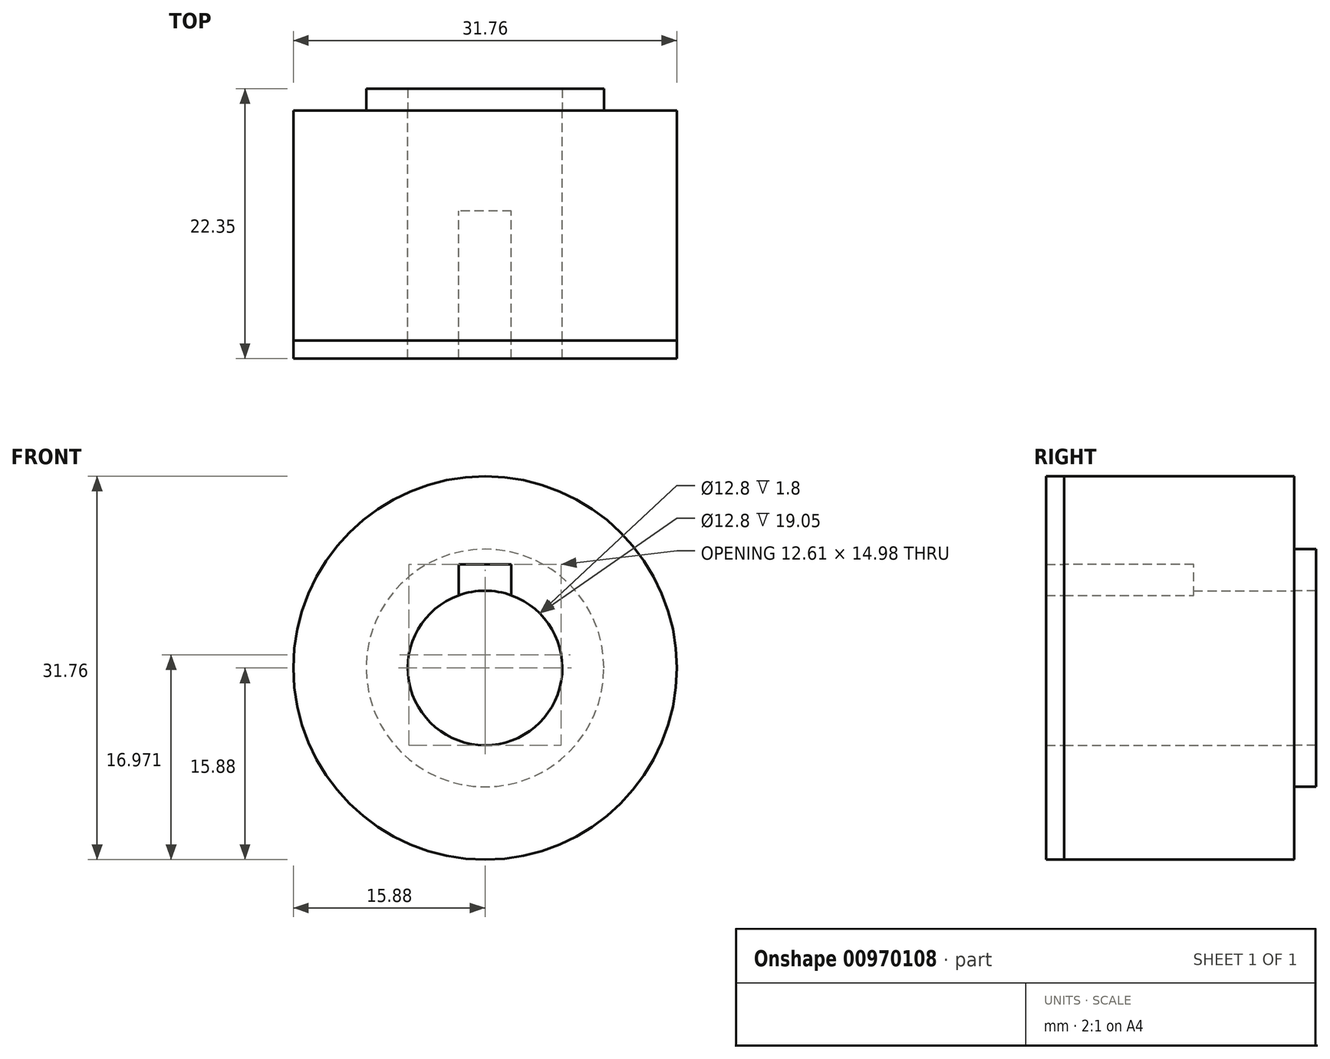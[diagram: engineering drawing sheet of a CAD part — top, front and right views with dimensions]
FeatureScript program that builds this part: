
annotation { "Feature Type Name" : "Feature", "Feature Type Description" : "" }
export const myFeature = defineFeature(function(context is Context, id is Id, definition is map)
    precondition{}
    {
        {
            var Q0;
            Q0=qCreatedBy(makeId("Front.planeOp"),FACE);
            var sketch = newSketch(context, id + "F0", { "sketchPlane" : qUnion([Q0])});
            skCircle(sketch, "E0", {"center": v(0, 0) * mm, "radius": 15.88 * mm});
            skCircle(sketch, "E1", {"center": v(0, 0) * mm, "radius": 6.4 * mm});
            skSolve(sketch);
        }
        {
            var Q0;
            Q0 = qSketchRegion(id + "F0", true);
            extrude(context, id + "F1", {"entities" : qUnion([Q0]), "depth" : 19.05 * mm, "offsetDistance" : 25.4 * mm});
        }
        {
            var Q0;
            Q0=makeQuery(id+"F1.opExtrude","CAP_FACE",FACE,{"disambiguationData":[OSD([sQuery(id+"F0.wireOp",EDGE,"E0"),sQuery(id+"F0.wireOp",EDGE,"E1")])],"isStart":false});
            var sketch = newSketch(context, id + "F2", { "sketchPlane" : qUnion([Q0])});
            skLineSegment(sketch, "E2", {"start": v(0, 6.4) * mm, "end": v(0, 4.22) * mm, "construction": true});
            skLineSegment(sketch, "E3.bottom", {"start": v(2.18, 4.22) * mm, "end": v(-2.18, 4.22) * mm});
            skLineSegment(sketch, "E3.top", {"start": v(2.18, 8.58) * mm, "end": v(-2.18, 8.58) * mm});
            skLineSegment(sketch, "E3.left", {"start": v(2.18, 4.22) * mm, "end": v(2.18, 8.58) * mm});
            skLineSegment(sketch, "E3.right", {"start": v(-2.18, 4.22) * mm, "end": v(-2.18, 8.58) * mm});
            skPoint(sketch, "E3.middle", {"position": v(0, 6.4) * mm});
            skSolve(sketch);
        }
        {
            var Q0;
            Q0 = qSketchRegion(id + "F2", true);
            extrude(context, id + "F3", {"entities" : qUnion([Q0]), "operationType" : NewBodyOperationType.REMOVE, "oppositeDirection" : true, "depth" : 10.72 * mm, "offsetDistance" : 25.4 * mm});
        }
        {
            var Q0;
            Q0=makeQuery(id+"F1.opExtrude","CAP_FACE",FACE,{"disambiguationData":[OSD([sQuery(id+"F0.wireOp",EDGE,"E0"),sQuery(id+"F0.wireOp",EDGE,"E1")])],"isStart":false});
            var sketch = newSketch(context, id + "F4", { "sketchPlane" : qUnion([Q0])});
            skCircle(sketch, "E4.0.0", {"center": v(0, 0) * mm, "radius": 15.88 * mm});
            skArc(sketch, "E5.0", {"start": v(-2.18, 6.02) * mm, "mid": v(0, -6.4) * mm, "end": v(2.18, 6.02) * mm});
            skLineSegment(sketch, "E6.0", {"start": v(-2.18, 6.02) * mm, "end": v(-2.18, 8.58) * mm});
            skLineSegment(sketch, "E7.0", {"start": v(2.18, 8.58) * mm, "end": v(-2.18, 8.58) * mm});
            skLineSegment(sketch, "E8.0", {"start": v(2.18, 6.02) * mm, "end": v(2.18, 8.58) * mm});
            skSolve(sketch);
        }
        {
            var Q0;
            Q0 = qSketchRegion(id + "F4", true);
            extrude(context, id + "F5", {"entities" : qUnion([Q0]), "depth" : 1.5 * mm, "offsetDistance" : 25.4 * mm});
        }
        {
            var Q0;
            Q0=makeQuery(id+"F1.opExtrude","CAP_FACE",FACE,{"disambiguationData":[OSD([sQuery(id+"F0.wireOp",EDGE,"E0"),sQuery(id+"F0.wireOp",EDGE,"E1")])],"isStart":true});
            var sketch = newSketch(context, id + "F6", { "sketchPlane" : qUnion([Q0])});
            skCircle(sketch, "E9.0", {"center": v(0, 0) * mm, "radius": 6.4 * mm});
            skCircle(sketch, "E10", {"center": v(0, 0) * mm, "radius": 9.84 * mm});
            skSolve(sketch);
        }
        {
            var Q0;
            Q0 = qSketchRegion(id + "F6", true);
            extrude(context, id + "F7", {"entities" : qUnion([Q0]), "depth" : 1.8 * mm, "offsetDistance" : 25.4 * mm});
        }
    });
